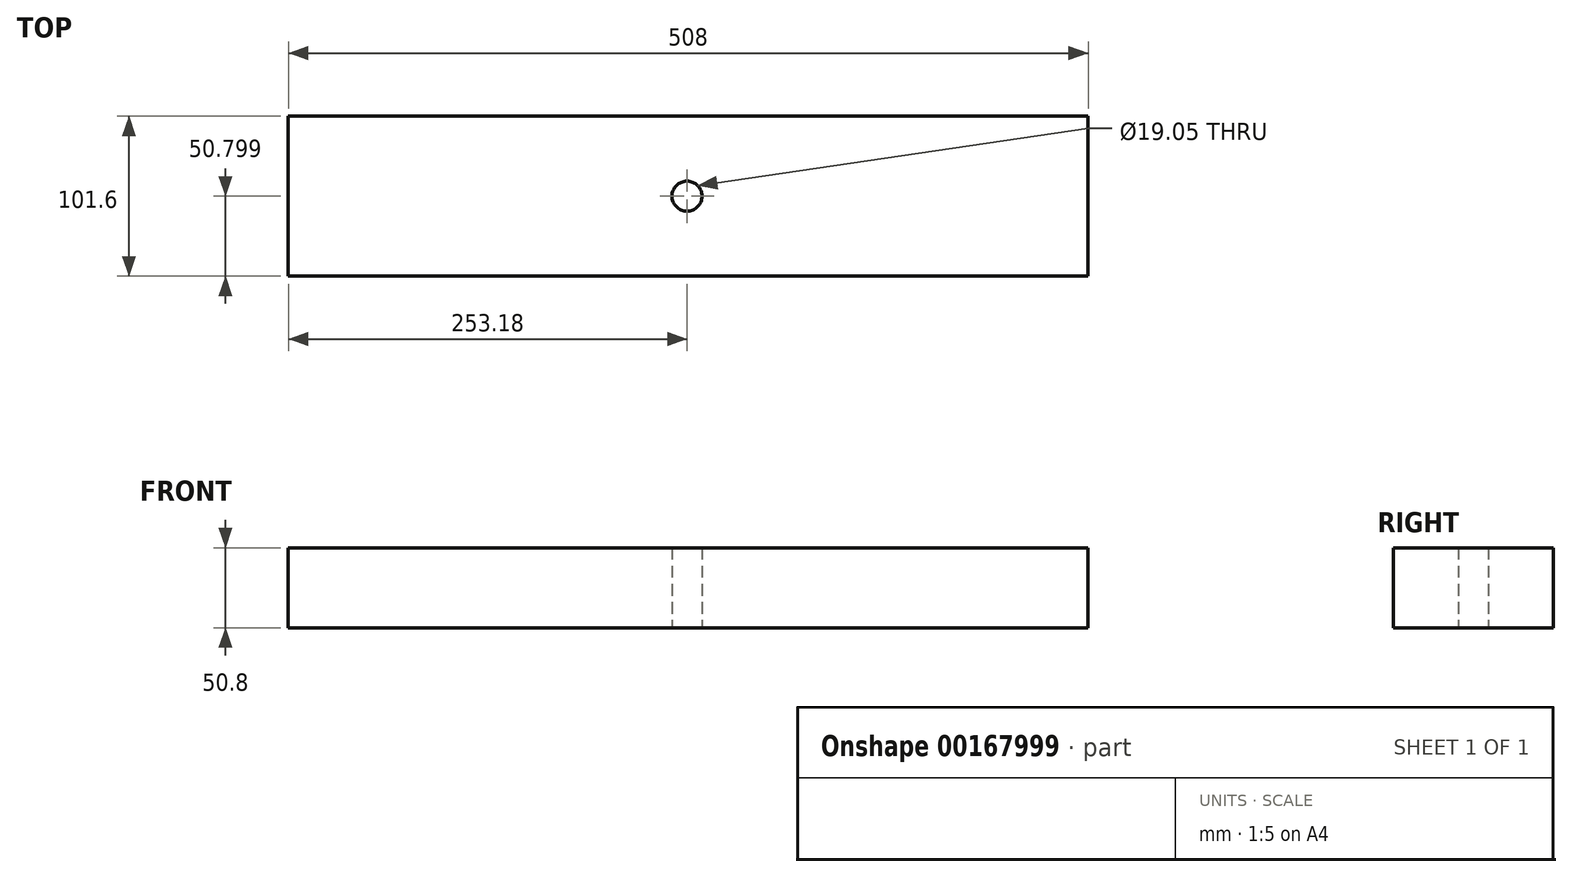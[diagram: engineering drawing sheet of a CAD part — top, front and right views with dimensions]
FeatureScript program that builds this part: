
annotation { "Feature Type Name" : "Feature", "Feature Type Description" : "" }
export const myFeature = defineFeature(function(context is Context, id is Id, definition is map)
    precondition{}
    {
        {
            var Q0;
            Q0=qCreatedBy(makeId("Top.planeOp"),FACE);
            var sketch = newSketch(context, id + "F0", { "sketchPlane" : qUnion([Q0])});
            skLineSegment(sketch, "E0.bottom", {"start": v(-253.18, 5.7) * mm, "end": v(254.82, 5.7) * mm});
            skLineSegment(sketch, "E0.top", {"start": v(-253.18, -95.9) * mm, "end": v(254.82, -95.9) * mm});
            skLineSegment(sketch, "E0.left", {"start": v(-253.18, 5.7) * mm, "end": v(-253.18, -95.9) * mm});
            skLineSegment(sketch, "E0.right", {"start": v(254.82, 5.7) * mm, "end": v(254.82, -95.9) * mm});
            skCircle(sketch, "E1", {"center": v(0, -45.1) * mm, "radius": 9.53 * mm});
            skSolve(sketch);
        }
        {
            var Q0;
            Q0=makeQuery(id+"F0.imprint","IMPRINT",FACE,{"disambiguationData":[TD([[makeQuery(id+"F0.imprint","IMPRINT",EDGE,{"derivedFrom":sQuery(id+"F0.wireOp",EDGE,"E0.bottom")}),-1.0]])]});
            extrude(context, id + "F1", {"entities" : qUnion([Q0]), "depth" : 50.8 * mm});
        }
    });
